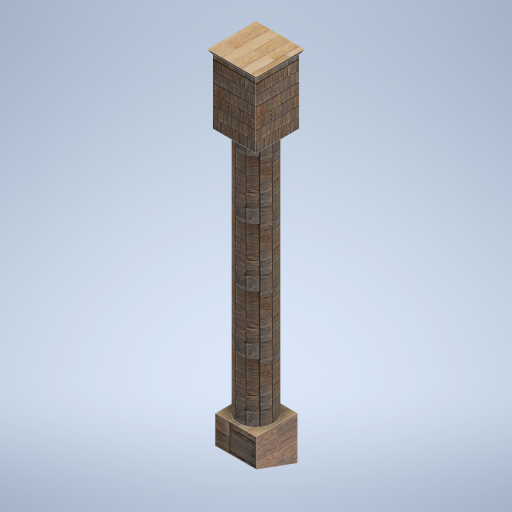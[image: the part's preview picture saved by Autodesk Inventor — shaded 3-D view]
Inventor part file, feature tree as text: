
AUTODESK INVENTOR PART (.ipt)
format: ipt  version: 2024.2 (Build 282272000, 272)  size: 351,744 bytes
history: native  units: in
note: dims shown in document units (in); Inventor stores cm internally (conversion verified against a paired STEP export)
features: sketch x5, other x3, plane x1
ambient origin geometry x8: Origin, YZ Plane, XZ Plane, XY Plane, X Axis, Y Axis, Z Axis, Center Point
bodies: Solid1 (feature_tree)
feature tree (9):
  other  "side_pillar_01_MIR.ipt"
  other  "Solid1::side_pillar_01_MIR.ipt"
  other  "TaggingFeature1"
  sketch  "Sketch1"  dims[d0=0.3937in]
  sketch  "Sketch2"
  sketch  "Sketch3"
  sketch  "Sketch4"
  sketch  "Sketch5"
  plane  "Work Plane3"
